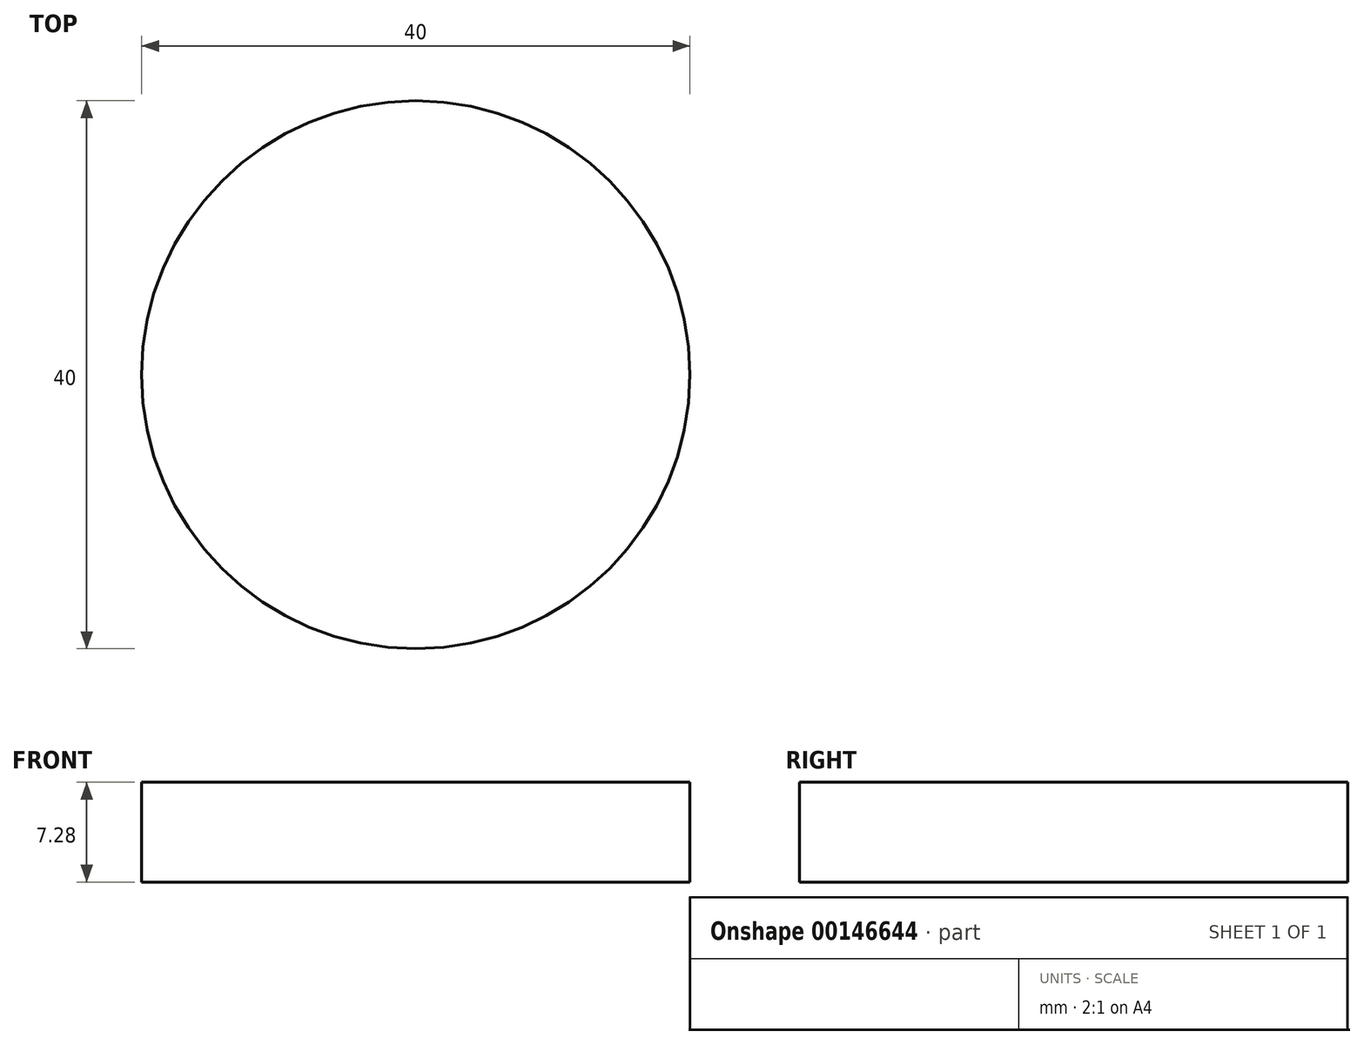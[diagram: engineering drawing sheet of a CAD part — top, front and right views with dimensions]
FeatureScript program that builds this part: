
annotation { "Feature Type Name" : "Feature", "Feature Type Description" : "" }
export const myFeature = defineFeature(function(context is Context, id is Id, definition is map)
    precondition{}
    {
        {
            var Q0;
            Q0=qCreatedBy(makeId("Top.planeOp"),FACE);
            var sketch = newSketch(context, id + "F0", { "sketchPlane" : qUnion([Q0])});
            skCircle(sketch, "E0", {"center": v(0, 0) * mm, "radius": 20 * mm});
            skSolve(sketch);
        }
        {
            var Q0;
            Q0=makeQuery(id+"F0.imprint","IMPRINT",FACE,{"disambiguationData":[TD([[makeQuery(id+"F0.imprint","IMPRINT",EDGE,{"derivedFrom":sQuery(id+"F0.wireOp",EDGE,"E0")}),1.0]])]});
            extrude(context, id + "F1", {"entities" : qUnion([Q0]), "depth" : 7.28 * mm});
        }
    });
